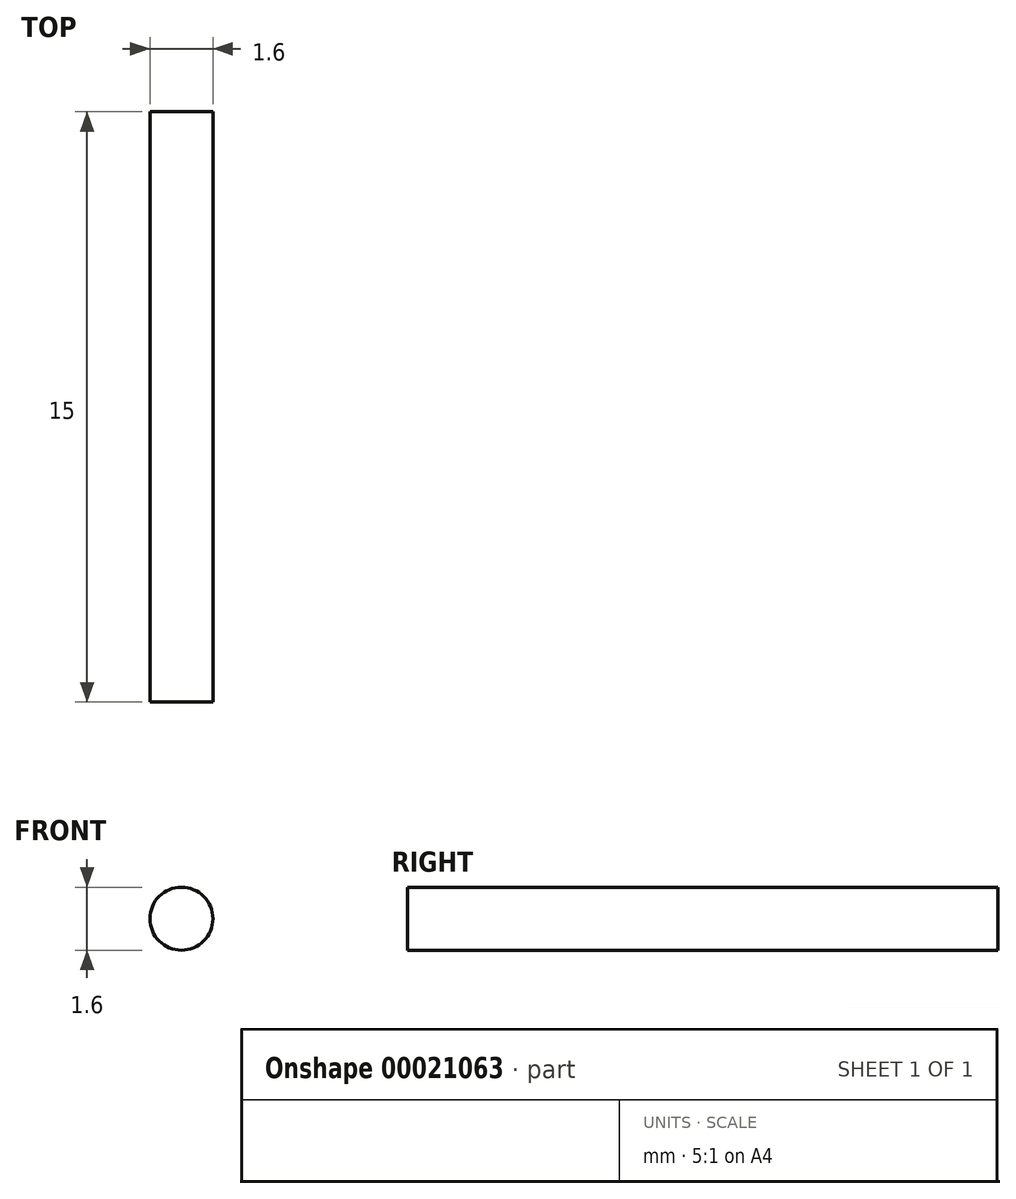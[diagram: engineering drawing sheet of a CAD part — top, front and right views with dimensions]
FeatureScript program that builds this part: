
annotation { "Feature Type Name" : "Feature", "Feature Type Description" : "" }
export const myFeature = defineFeature(function(context is Context, id is Id, definition is map)
    precondition{}
    {
        {
            var Q0;
            Q0=qCreatedBy(makeId("Front.planeOp"),FACE);
            var sketch = newSketch(context, id + "F0", { "sketchPlane" : qUnion([Q0])});
            skCircle(sketch, "E0", {"center": v(0, 0) * mm, "radius": 0.8 * mm});
            skSolve(sketch);
        }
        {
            var Q0;
            Q0=makeQuery(id+"F0.imprint","IMPRINT",FACE,{"disambiguationData":[TD([[makeQuery(id+"F0.imprint","IMPRINT",EDGE,{"derivedFrom":sQuery(id+"F0.wireOp",EDGE,"E0")}),1.0]])]});
            extrude(context, id + "F1", {"entities" : qUnion([Q0]), "depth" : 15 * mm});
        }
    });
